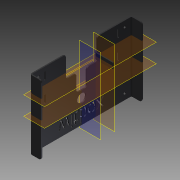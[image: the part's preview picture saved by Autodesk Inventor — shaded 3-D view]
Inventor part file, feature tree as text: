
AUTODESK INVENTOR PART (.ipt)
format: ipt  version: 2015 (Build 190159000, 159)  size: 680,960 bytes
history: native  units: mm
features: extrude x12, projected_geometry x6, fillet x4, hole x3, plane x3, other x1
ambient origin geometry x8: Origin, YZ Plane, XZ Plane, XY Plane, X Axis, Y Axis, Z Axis, Center Point
bodies: Solid1 (feature_tree)
feature tree (29):
  extrude  "Extrusión1"  Depth=16.0mm
  fillet  "Empalme1"  Radius=8.0mm
  extrude  "Extrusión2"  Depth=100.0mm
  hole  "Agujero1"  [1 undecoded]
  extrude  "Extrusión4"  Depth=2.0mm
  hole  "Agujero2"  [1 undecoded]
  extrude  "Extrusión5"  Depth=2.0mm
  fillet  "Empalme3"  Radius=0.2mm
  hole  "aGUJEROS SOS"  [1 undecoded]
  extrude  "Extrusión9"  Depth=3.0mm
  extrude  "Extrusión10"  Depth=10.11138mm
  extrude  "Extrusión11"  Depth=120.0mm TaperAngle=0.0deg
  extrude  "Extrusión12"  Depth=4.0mm
  extrude  "Extrusión13"  Depth=10.11138mm
  plane  "Plano de trabajo1"
  extrude  "Extrusión14"  Depth=100.0mm
  fillet  "Empalme4"  Radius=25.2mm
  extrude  "Extrusión15"  Depth=105.0mm
  fillet  "Empalme5"  Radius=5.0mm
  extrude  "Extrusión16"  Depth=120.0mm
  plane  "Plano de trabajo2"
  plane  "Plano de trabajo3"
  projected_geometry  "Contorno proyectado1"
  projected_geometry  "Contorno proyectado2"
  projected_geometry  "Contorno proyectado9"
  projected_geometry  "Contorno proyectado10"
  projected_geometry  "Contorno proyectado11"
  projected_geometry  "Contorno proyectado12"
  other  "Definición1"
note: 3 required parameter values undecoded (feature->parameter linkage not recoverable at this tier; creation-order binding heuristic only, values carry confidence <= 0.55)
